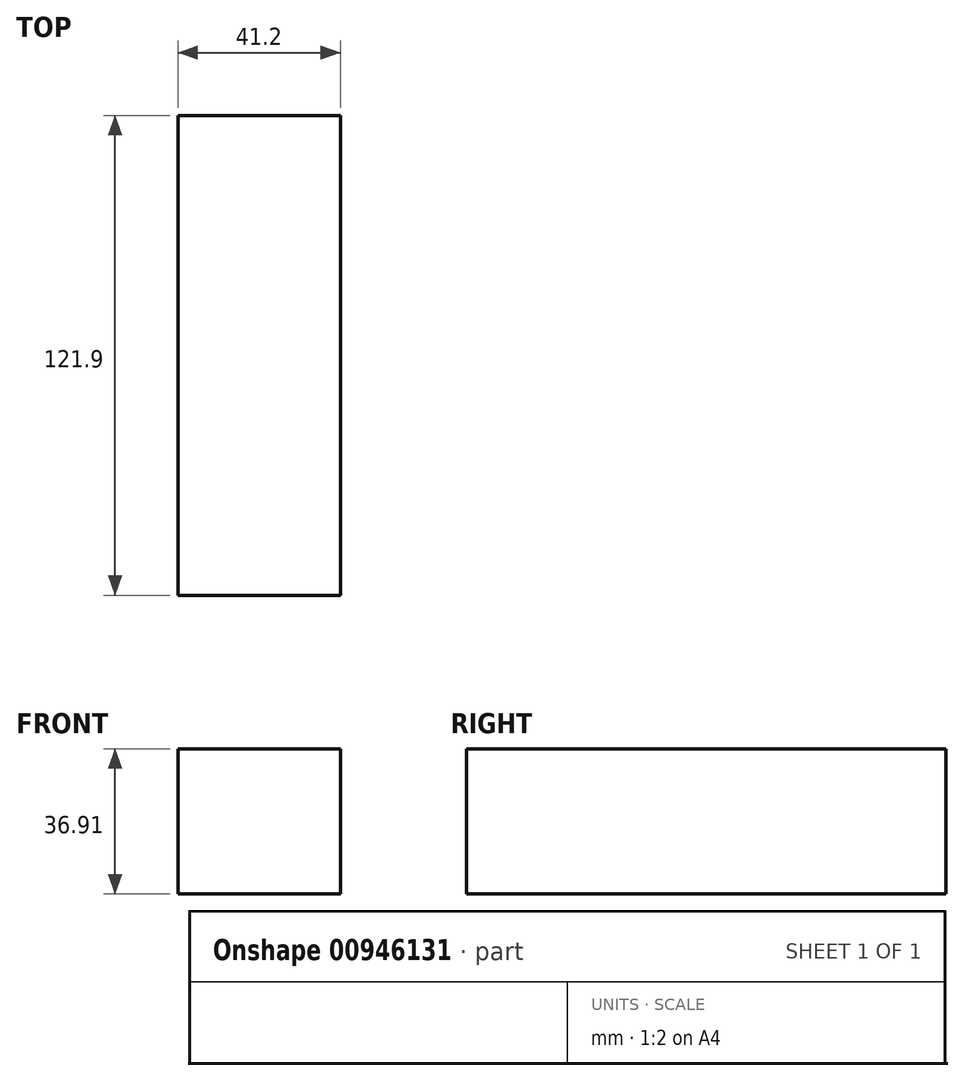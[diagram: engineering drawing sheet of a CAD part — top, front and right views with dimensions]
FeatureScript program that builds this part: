
annotation { "Feature Type Name" : "Feature", "Feature Type Description" : "" }
export const myFeature = defineFeature(function(context is Context, id is Id, definition is map)
    precondition{}
    {
        {
            var Q0;
            Q0=qCreatedBy(makeId("Front.planeOp"),FACE);
            var sketch = newSketch(context, id + "F0", { "sketchPlane" : qUnion([Q0])});
            skLineSegment(sketch, "E0.bottom", {"start": v(-98.92, 58.1) * mm, "end": v(-57.72, 58.1) * mm});
            skLineSegment(sketch, "E0.top", {"start": v(-98.92, 21.18) * mm, "end": v(-57.72, 21.18) * mm});
            skLineSegment(sketch, "E0.left", {"start": v(-98.92, 58.1) * mm, "end": v(-98.92, 21.18) * mm});
            skLineSegment(sketch, "E0.right", {"start": v(-57.72, 58.1) * mm, "end": v(-57.72, 21.18) * mm});
            skSolve(sketch);
        }
        {
            var Q0;
            Q0 = qSketchRegion(id + "F0", true);
            extrude(context, id + "F1", {"entities" : qUnion([Q0]), "depth" : 121.9 * mm, "offsetDistance" : 25 * mm});
        }
    });
